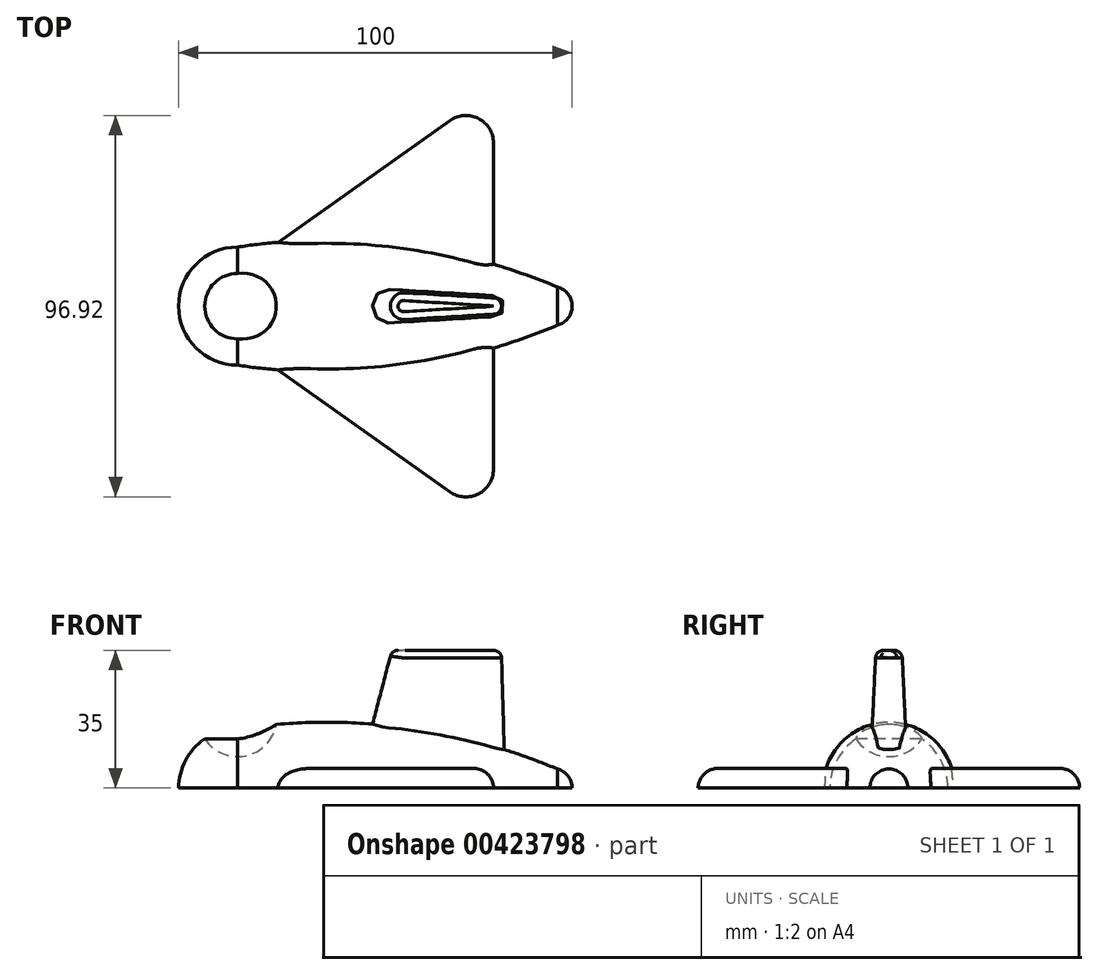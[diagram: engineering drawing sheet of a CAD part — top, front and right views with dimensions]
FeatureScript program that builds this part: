
annotation { "Feature Type Name" : "Feature", "Feature Type Description" : "" }
export const myFeature = defineFeature(function(context is Context, id is Id, definition is map)
    precondition{}
    {
        {
            var Q0;
            Q0=qCreatedBy(makeId("Top.planeOp"),FACE);
            var sketch = newSketch(context, id + "F0", { "sketchPlane" : qUnion([Q0])});
            skArc(sketch, "E0", {"start": v(0, 15) * mm, "mid": v(-10.6, 10.6) * mm, "end": v(-15, 0) * mm});
            skArc(sketch, "E1", {"start": v(85, 0) * mm, "mid": v(83.95, 3.07) * mm, "end": v(81.23, 4.85) * mm});
            skLineSegment(sketch, "E2", {"start": v(-45.79, 0) * mm, "end": v(96.26, 0) * mm, "construction": true});
            skLineSegment(sketch, "E3", {"start": v(-15, 0) * mm, "end": v(85, 0) * mm});
            skArc(sketch, "E4", {"start": v(81.23, 4.85) * mm, "mid": v(41.32, 15.57) * mm, "end": v(0, 15) * mm});
            skSolve(sketch);
        }
        {
            var Q0;
            Q0=makeQuery(id+"F0.imprint","IMPRINT",FACE,{"disambiguationData":[TD([[makeQuery(id+"F0.imprint","IMPRINT",EDGE,{"derivedFrom":sQuery(id+"F0.wireOp",EDGE,"E0")}),1.0]])]});
            var Q1;
            Q1=sQuery(id+"F0.wireOp",EDGE,"E3");
            revolve(context, id + "F1", {"entities" : qUnion([Q0]), "axis" : qUnion([Q1]), "revolveType" : RevolveType.ONE_DIRECTION, "angle" : 180 * degree});
        }
        {
            var Q0;
            Q0=qCreatedBy(makeId("Front.planeOp"),FACE);
            var sketch = newSketch(context, id + "F2", { "sketchPlane" : qUnion([Q0])});
            skArc(sketch, "E5", {"start": v(10, 18) * mm, "mid": v(0, 28) * mm, "end": v(-10, 18) * mm});
            skLineSegment(sketch, "E6", {"start": v(-10, 18) * mm, "end": v(10, 18) * mm});
            skSolve(sketch);
        }
        {
            var Q0;
            Q0=makeQuery(id+"F2.imprint","IMPRINT",FACE,{"disambiguationData":[TD([[makeQuery(id+"F2.imprint","IMPRINT",EDGE,{"derivedFrom":sQuery(id+"F2.wireOp",EDGE,"E5")}),1.0]])]});
            var Q1;
            Q1=sQuery(id+"F2.wireOp",EDGE,"E6");
            revolve(context, id + "F3", {"operationType" : NewBodyOperationType.REMOVE, "entities" : qUnion([Q0]), "axis" : qUnion([Q1]), "revolveType" : RevolveType.FULL, "oppositeDirection" : true});
        }
        {
            var Q0;
            Q0=qCreatedBy(makeId("Top.planeOp"),FACE);
            var sketch = newSketch(context, id + "F4", { "sketchPlane" : qUnion([Q0])});
            skArc(sketch, "E7", {"start": v(35.33, 4.99) * mm, "mid": v(30, 0) * mm, "end": v(35.33, -4.99) * mm});
            skArc(sketch, "E8", {"start": v(65.2, -3) * mm, "mid": v(68, 0) * mm, "end": v(65.2, 3) * mm});
            skLineSegment(sketch, "E9", {"start": v(35.33, 4.99) * mm, "end": v(65.2, 3) * mm});
            skLineSegment(sketch, "E10", {"start": v(35.33, -4.99) * mm, "end": v(65.2, -3) * mm});
            skSolve(sketch);
        }
        {
            var Q0;
            Q0=qCreatedBy(makeId("Top.planeOp"),FACE);
            cPlane(context, id + "F5", {"entities" : qUnion([Q0]), "cplaneType" : CPlaneType.OFFSET, "offset" : 35 * mm, "width" : 150 * mm, "height" : 150 * mm});
        }
        {
            var Q0;
            Q0=qCreatedBy(id+"F5.planeOp",FACE);
            var sketch = newSketch(context, id + "F6", { "sketchPlane" : qUnion([Q0])});
            skPoint(sketch, "E11.0", {"position": v(65, 0) * mm});
            skArc(sketch, "E12", {"start": v(65.12, -2) * mm, "mid": v(67, 0) * mm, "end": v(65.12, 2) * mm});
            skArc(sketch, "E13", {"start": v(42.7, 3.3) * mm, "mid": v(39.2, 0) * mm, "end": v(42.7, -3.3) * mm});
            skLineSegment(sketch, "E14", {"start": v(42.7, 3.3) * mm, "end": v(65.12, 2) * mm});
            skLineSegment(sketch, "E15", {"start": v(42.7, -3.3) * mm, "end": v(65.12, -2) * mm});
            skSolve(sketch);
        }
        {
            var Q1;
            Q1=makeQuery(id+"F4.imprint","IMPRINT",FACE,{"disambiguationData":[TD([[makeQuery(id+"F4.imprint","IMPRINT",EDGE,{"derivedFrom":sQuery(id+"F4.wireOp",EDGE,"E7")}),1.0]])]});
            var Q2;
            Q2=makeQuery(id+"F6.imprint","IMPRINT",FACE,{"disambiguationData":[TD([[makeQuery(id+"F6.imprint","IMPRINT",EDGE,{"derivedFrom":sQuery(id+"F6.wireOp",EDGE,"E12")}),1.0]])]});
            loft(context, id + "F7", {"operationType" : NewBodyOperationType.ADD, "sheetProfilesArray" : [{ "sheetProfileEntities" : qUnion([Q1]) }, { "sheetProfileEntities" : qUnion([Q2]) }]});
        }
        {
            var Q0;
            Q0=qCreatedBy(makeId("Top.planeOp"),FACE);
            var sketch = newSketch(context, id + "F8", { "sketchPlane" : qUnion([Q0])});
            skLineSegment(sketch, "E16", {"start": v(5, 12.47) * mm, "end": v(53.95, 47.17) * mm});
            skPoint(sketch, "E17.orphan", {"position": v(-3.8, 6.24) * mm});
            skLineSegment(sketch, "E18", {"start": v(65, 41.46) * mm, "end": v(65, 6) * mm});
            skPoint(sketch, "E19.visualSharp", {"position": v(65, 55) * mm});
            skArc(sketch, "E19.filletArc", {"start": v(65, 41.46) * mm, "mid": v(61.21, 47.68) * mm, "end": v(53.95, 47.17) * mm});
            skPoint(sketch, "E20.orphan", {"position": v(81.23, 4.85) * mm});
            skPoint(sketch, "E21.orphan", {"position": v(0, 15) * mm});
            skArc(sketch, "E22", {"start": v(65, 6) * mm, "mid": v(35.12, 10.39) * mm, "end": v(5, 12.47) * mm});
            skSolve(sketch);
        }
        {
            var Q0;
            Q0=makeQuery(id+"F8.imprint","IMPRINT",FACE,{"disambiguationData":[TD([[makeQuery(id+"F8.imprint","IMPRINT",EDGE,{"derivedFrom":sQuery(id+"F8.wireOp",EDGE,"E16")}),-1.0]])]});
            extrude(context, id + "F9", {"entities" : qUnion([Q0]), "operationType" : NewBodyOperationType.ADD, "depth" : 5 * mm});
        }
        {
            var Q0;
            Q0=makeQuery(id+"F1.opRevolve","SWEPT_BODY",BODY,{"disambiguationData":[OSD([sQuery(id+"F0.wireOp",EDGE,"E0"),sQuery(id+"F0.wireOp",EDGE,"E1"),sQuery(id+"F0.wireOp",EDGE,"3OhW7JyN-gsDZ-XPBF-qmex-Y5adJNZ3217h"),sQuery(id+"F0.wireOp",EDGE,"E3")])]});
            var Q1;
            Q1=qCreatedBy(makeId("Front.planeOp"),FACE);
            mirror(context, id + "F10", {"operationType" : NewBodyOperationType.ADD, "entities" : qUnion([Q0]), "mirrorPlane" : qUnion([Q1])});
        }
        {
            var Q0;
            Q0=makeQuery(id+"F9.opExtrude","CAP_EDGE",EDGE,{"disambiguationData":[OSD([sQuery(id+"F8.wireOp",EDGE,"E16")])],"isStart":false});
            var Q1;
            Q1=makeQuery(id+"F10.opPattern","COPY",EDGE,{"derivedFrom":makeQuery(id+"F9.opExtrude","CAP_EDGE",EDGE,{"disambiguationData":[OSD([sQuery(id+"F8.wireOp",EDGE,"E16")])],"isStart":false}),"instanceName":"1"});
            fillet(context, id + "F11", {"entities" : qUnion([Q0, Q1]), "radius" : 5 * mm, "tangentPropagation" : true, "allowEdgeOverflow" : false});
        }
        {
            var Q0;
            Q0=makeQuery(id+"F7.opLoft","MID_CAP_EDGE",EDGE,{"disambiguationData":[OSD([sQuery(id+"F6.wireOp",EDGE,"E13"),sQuery(id+"F6.wireOp",EDGE,"E14"),sQuery(id+"F6.wireOp",EDGE,"E15")])],"capPos":1.0});
            var Q1;
            Q1=makeQuery(id+"F7.boolean.opBoolean","INTERSECT",EDGE,{"derivedFrom":[makeQuery(id+"F1.opRevolve","SWEPT_FACE",FACE,{"disambiguationData":[OSD([sQuery(id+"F0.wireOp",EDGE,"3OhW7JyN-gsDZ-XPBF-qmex-Y5adJNZ3217h")])]}),makeQuery(id+"F7.opLoft","SWEPT_FACE",FACE,{"disambiguationData":[OSD([sQuery(id+"F4.wireOp",EDGE,"E7"),sQuery(id+"F4.wireOp",EDGE,"E9"),sQuery(id+"F4.wireOp",EDGE,"E10"),sQuery(id+"F6.wireOp",EDGE,"E13"),sQuery(id+"F6.wireOp",EDGE,"E14"),sQuery(id+"F6.wireOp",EDGE,"E15")])]})]});
            fillet(context, id + "F12", {"entities" : qUnion([Q0, Q1]), "radius" : 2 * mm, "tangentPropagation" : true, "allowEdgeOverflow" : false});
        }
    });
